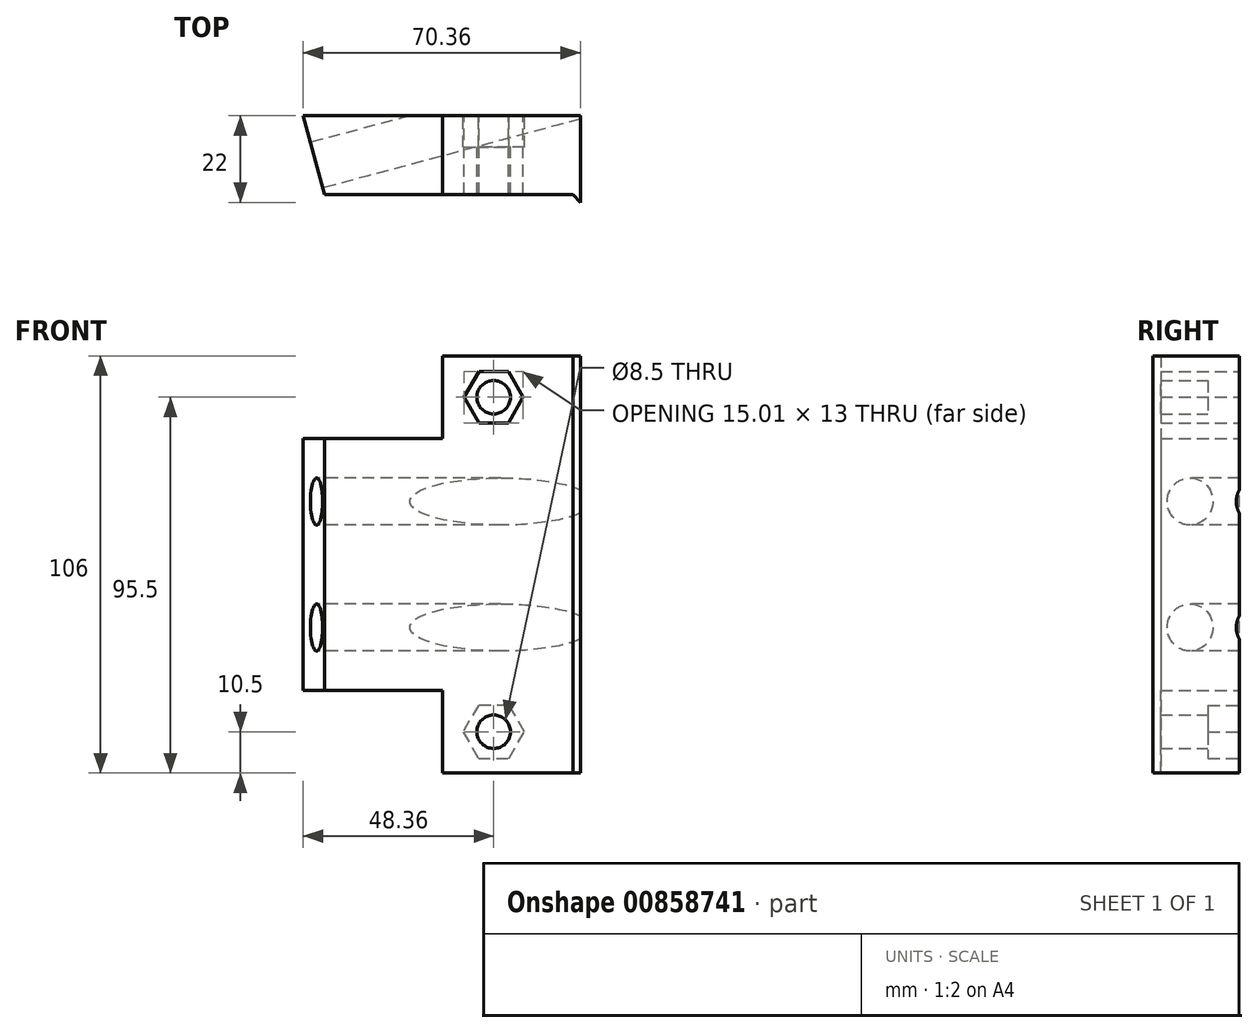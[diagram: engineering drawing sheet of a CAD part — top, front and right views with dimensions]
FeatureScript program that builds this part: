
annotation { "Feature Type Name" : "Feature", "Feature Type Description" : "" }
export const myFeature = defineFeature(function(context is Context, id is Id, definition is map)
    precondition{}
    {
        {
            var Q0;
            Q0=qCreatedBy(makeId("Top.planeOp"),FACE);
            var sketch = newSketch(context, id + "F0", { "sketchPlane" : qUnion([Q0])});
            skLineSegment(sketch, "E0", {"start": v(-1.9, 0) * mm, "end": v(-65, 0) * mm});
            skLineSegment(sketch, "E1", {"start": v(-65, 0) * mm, "end": v(-70.36, 20) * mm});
            skLineSegment(sketch, "E2", {"start": v(-70.36, 20) * mm, "end": v(0, 20) * mm});
            skLineSegment(sketch, "E3", {"start": v(-1.9, 0) * mm, "end": v(0, -2) * mm});
            skLineSegment(sketch, "E4", {"start": v(0, 20) * mm, "end": v(0, -2) * mm});
            skSolve(sketch);
        }
        {
            var Q0;
            Q0=makeQuery(id+"F0.imprint","IMPRINT",FACE,{"disambiguationData":[TD([[makeQuery(id+"F0.imprint","IMPRINT",EDGE,{"derivedFrom":sQuery(id+"F0.wireOp",EDGE,"E0")}),-1.0]])]});
            extrude(context, id + "F1", {"entities" : qUnion([Q0]), "depth" : 64 * mm, "offsetDistance" : 25 * mm});
        }
        {
            var Q0;
            Q0=makeQuery(id+"F1.opExtrude","SWEPT_FACE",FACE,{"disambiguationData":[OSD([sQuery(id+"F0.wireOp",EDGE,"E1")])]});
            var sketch = newSketch(context, id + "F2", { "sketchPlane" : qUnion([Q0])});
            skLineSegment(sketch, "E5", {"start": v(-24.53, 64) * mm, "end": v(-24.53, 0) * mm});
            skLineSegment(sketch, "E6", {"start": v(-24.53, 16) * mm, "end": v(-48.69, 16) * mm});
            skLineSegment(sketch, "E7", {"start": v(-48.69, 16) * mm, "end": v(-48.69, 48) * mm});
            skLineSegment(sketch, "E8", {"start": v(-48.69, 48) * mm, "end": v(-24.53, 48) * mm});
            skSolve(sketch);
        }
        {
            var Q0;
            Q0=sQuery(id+"F2.wireOp",VERTEX,"E8.end");
            var Q1;
            Q1=sQuery(id+"F2.wireOp",VERTEX,"E6.start");
            var Q2;
            Q2=makeQuery(id+"F1.opExtrude","SWEPT_BODY",BODY,{"disambiguationData":[OSD([sQuery(id+"F0.wireOp",EDGE,"E0"),sQuery(id+"F0.wireOp",EDGE,"E1"),sQuery(id+"F0.wireOp",EDGE,"E2"),sQuery(id+"F0.wireOp",EDGE,"E3"),sQuery(id+"F0.wireOp",EDGE,"E4")])]});
            hole(context, id + "F3", {"style" : HoleStyle.SIMPLE, "endStyle" : HoleEndStyle.THROUGH, "holeDiameter" : 12 * mm, "majorDiameter" : 5 * mm, "isTappedThrough" : true, "tappedDepth" : 12 * mm, "tapClearance" : 3, "locations" : qUnion([Q0, Q1]), "scope" : qUnion([Q2])});
        }
        {
            var Q0;
            Q0=makeQuery(id+"F1.opExtrude","CAP_FACE",FACE,{"disambiguationData":[OSD([sQuery(id+"F0.wireOp",EDGE,"E0"),sQuery(id+"F0.wireOp",EDGE,"E1"),sQuery(id+"F0.wireOp",EDGE,"E2"),sQuery(id+"F0.wireOp",EDGE,"E3"),sQuery(id+"F0.wireOp",EDGE,"E4")])],"isStart":true});
            var sketch = newSketch(context, id + "F4", { "sketchPlane" : qUnion([Q0])});
            skLineSegment(sketch, "E9.bottom", {"start": v(0, -20) * mm, "end": v(-35, -20) * mm});
            skLineSegment(sketch, "E9.top", {"start": v(0, 0) * mm, "end": v(-35, 0) * mm});
            skLineSegment(sketch, "E9.left", {"start": v(0, -20) * mm, "end": v(0, 0) * mm});
            skLineSegment(sketch, "E9.right", {"start": v(-35, -20) * mm, "end": v(-35, 0) * mm});
            skSolve(sketch);
        }
        {
            var Q0;
            Q0=makeQuery(id+"F4.imprint","IMPRINT",FACE,{"disambiguationData":[TD([[makeQuery(id+"F4.imprint","IMPRINT",EDGE,{"derivedFrom":sQuery(id+"F4.wireOp",EDGE,"E9.bottom")}),1.0]])]});
            var Q1;
            {var subQ1=makeQuery(id+"F1.opExtrude","CAP_EDGE",EDGE,{"disambiguationData":[OSD([sQuery(id+"F0.wireOp",EDGE,"E3")])],"isStart":true});Q1=makeQuery(id+"F4.imprint","IMPRINT",FACE,{"disambiguationData":[TD([[makeQuery(id+"F4.imprint","IMPRINT",EDGE,{"derivedFrom":subQ1}),-1.0]])]});}
            extrude(context, id + "F5", {"entities" : qUnion([Q0, Q1]), "operationType" : NewBodyOperationType.ADD, "depth" : 21 * mm, "offsetDistance" : 25 * mm});
        }
        {
            var Q0;
            Q0=makeQuery(id+"F5.boolean.opBoolean","MERGE",FACE,{"derivedFrom":[makeQuery(id+"F1.opExtrude","SWEPT_FACE",FACE,{"disambiguationData":[OSD([sQuery(id+"F0.wireOp",EDGE,"E2")])]}),makeQuery(id+"F5.opExtrude","SWEPT_FACE",FACE,{"disambiguationData":[OSD([sQuery(id+"F4.wireOp",EDGE,"E9.bottom")])]})]});
            var sketch = newSketch(context, id + "F6", { "sketchPlane" : qUnion([Q0])});
            skLineSegment(sketch, "E10", {"start": v(35, -10.5) * mm, "end": v(0, -10.5) * mm});
            skLineSegment(sketch, "E11", {"start": v(22, -10.5) * mm, "end": v(22, -21) * mm});
            skCircle(sketch, "E12.cCircle", {"center": v(22, -10.5) * mm, "radius": 6.75 * mm, "construction": true});
            skLineSegment(sketch, "E12.0", {"start": v(25.9, -17.25) * mm, "end": v(18.1, -17.25) * mm});
            skLineSegment(sketch, "E12.1", {"start": v(18.1, -17.25) * mm, "end": v(14.2, -10.5) * mm});
            skLineSegment(sketch, "E12.2", {"start": v(14.2, -10.5) * mm, "end": v(18.1, -3.75) * mm});
            skLineSegment(sketch, "E12.3", {"start": v(18.1, -3.75) * mm, "end": v(25.9, -3.75) * mm});
            skLineSegment(sketch, "E12.4", {"start": v(25.9, -3.75) * mm, "end": v(29.8, -10.5) * mm});
            skLineSegment(sketch, "E12.5", {"start": v(29.8, -10.5) * mm, "end": v(25.9, -17.25) * mm});
            skPoint(sketch, "E12.0.midPoint", {"position": v(22, -17.25) * mm});
            skSolve(sketch);
        }
        {
            var Q0;
            {var subQ3=sQuery(id+"F6.wireOp",EDGE,"E12.5");Q0=makeQuery(id+"F6.imprint","IMPRINT",FACE,{"disambiguationData":[TD([[makeQuery(id+"F6.imprint","IMPRINT",EDGE,{"derivedFrom":subQ3}),-1.0]])]});}
            var Q1;
            {var subQ0=sQuery(id+"F6.wireOp",EDGE,"E12.2");Q1=makeQuery(id+"F6.imprint","IMPRINT",FACE,{"disambiguationData":[TD([[makeQuery(id+"F6.imprint","IMPRINT",EDGE,{"derivedFrom":subQ0}),-1.0]])]});}
            var Q2;
            {var subQ3=sQuery(id+"F6.wireOp",EDGE,"E12.1");Q2=makeQuery(id+"F6.imprint","IMPRINT",FACE,{"disambiguationData":[TD([[makeQuery(id+"F6.imprint","IMPRINT",EDGE,{"derivedFrom":subQ3}),-1.0]])]});}
            extrude(context, id + "F7", {"entities" : qUnion([Q0, Q1, Q2]), "operationType" : NewBodyOperationType.REMOVE, "oppositeDirection" : true, "depth" : 8 * mm, "offsetDistance" : 25 * mm});
        }
        {
            var Q0;
            Q0=makeQuery(id+"F1.opExtrude","CAP_FACE",FACE,{"disambiguationData":[OSD([sQuery(id+"F0.wireOp",EDGE,"E0"),sQuery(id+"F0.wireOp",EDGE,"E1"),sQuery(id+"F0.wireOp",EDGE,"E2"),sQuery(id+"F0.wireOp",EDGE,"E3"),sQuery(id+"F0.wireOp",EDGE,"E4")])],"isStart":false});
            var sketch = newSketch(context, id + "F8", { "sketchPlane" : qUnion([Q0])});
            skLineSegment(sketch, "E13.bottom", {"start": v(0, 20) * mm, "end": v(-35, 20) * mm});
            skLineSegment(sketch, "E13.top", {"start": v(0, 0) * mm, "end": v(-35, 0) * mm});
            skLineSegment(sketch, "E13.left", {"start": v(0, 20) * mm, "end": v(0, 0) * mm});
            skLineSegment(sketch, "E13.right", {"start": v(-35, 20) * mm, "end": v(-35, 0) * mm});
            skSolve(sketch);
        }
        {
            var Q0;
            Q0=makeQuery(id+"F8.imprint","IMPRINT",FACE,{"disambiguationData":[TD([[makeQuery(id+"F8.imprint","IMPRINT",EDGE,{"derivedFrom":sQuery(id+"F8.wireOp",EDGE,"E13.bottom")}),-1.0]])]});
            var Q1;
            {var subQ1=makeQuery(id+"F1.opExtrude","CAP_EDGE",EDGE,{"disambiguationData":[OSD([sQuery(id+"F0.wireOp",EDGE,"E3")])],"isStart":false});Q1=makeQuery(id+"F8.imprint","IMPRINT",FACE,{"disambiguationData":[TD([[makeQuery(id+"F8.imprint","IMPRINT",EDGE,{"derivedFrom":subQ1}),1.0]])]});}
            extrude(context, id + "F9", {"entities" : qUnion([Q0, Q1]), "operationType" : NewBodyOperationType.ADD, "depth" : 21 * mm, "offsetDistance" : 25 * mm});
        }
        {
            var Q0;
            Q0=makeQuery(id+"F9.boolean.opBoolean","MERGE",FACE,{"derivedFrom":[makeQuery(id+"F5.boolean.opBoolean","MERGE",FACE,{"derivedFrom":[makeQuery(id+"F1.opExtrude","SWEPT_FACE",FACE,{"disambiguationData":[OSD([sQuery(id+"F0.wireOp",EDGE,"E2")])]}),makeQuery(id+"F5.opExtrude","SWEPT_FACE",FACE,{"disambiguationData":[OSD([sQuery(id+"F4.wireOp",EDGE,"E9.bottom")])]})]}),makeQuery(id+"F9.opExtrude","SWEPT_FACE",FACE,{"disambiguationData":[OSD([sQuery(id+"F8.wireOp",EDGE,"E13.bottom")])]})]});
            var sketch = newSketch(context, id + "F10", { "sketchPlane" : qUnion([Q0])});
            skLineSegment(sketch, "E14", {"start": v(35, 74.5) * mm, "end": v(0, 74.5) * mm});
            skCircle(sketch, "E15.cCircle", {"center": v(22, 74.5) * mm, "radius": 6.5 * mm, "construction": true});
            skPoint(sketch, "E15.cCircle.centerSnap0", {"position": v(22, -17.25) * mm});
            skLineSegment(sketch, "E15.0", {"start": v(25.75, 68) * mm, "end": v(18.25, 68) * mm});
            skLineSegment(sketch, "E15.1", {"start": v(18.25, 68) * mm, "end": v(14.5, 74.5) * mm});
            skLineSegment(sketch, "E15.2", {"start": v(14.5, 74.5) * mm, "end": v(18.25, 81) * mm});
            skLineSegment(sketch, "E15.3", {"start": v(18.25, 81) * mm, "end": v(25.75, 81) * mm});
            skLineSegment(sketch, "E15.4", {"start": v(25.75, 81) * mm, "end": v(29.5, 74.5) * mm});
            skLineSegment(sketch, "E15.5", {"start": v(29.5, 74.5) * mm, "end": v(25.75, 68) * mm});
            skPoint(sketch, "E15.0.midPoint", {"position": v(22, 68) * mm});
            skSolve(sketch);
        }
        {
            var Q0;
            Q0=makeQuery(id+"F10.imprint","IMPRINT",FACE,{"disambiguationData":[TD([[makeQuery(id+"F10.imprint","IMPRINT",EDGE,{"derivedFrom":sQuery(id+"F10.wireOp",EDGE,"E15.0")}),-1.0]])]});
            var Q1;
            {var subQ0=sQuery(id+"F10.wireOp",EDGE,"E15.2");Q1=makeQuery(id+"F10.imprint","IMPRINT",FACE,{"disambiguationData":[TD([[makeQuery(id+"F10.imprint","IMPRINT",EDGE,{"derivedFrom":subQ0}),-1.0]])]});}
            extrude(context, id + "F11", {"entities" : qUnion([Q0, Q1]), "operationType" : NewBodyOperationType.REMOVE, "oppositeDirection" : true, "depth" : 8 * mm, "offsetDistance" : 25 * mm});
        }
        {
            var Q0;
            Q0=makeQuery(id+"F11.boolean.opBoolean","COPY",FACE,{"derivedFrom":makeQuery(id+"F11.opExtrude","CAP_FACE",FACE,{"disambiguationData":[OSD([sQuery(id+"F10.wireOp",EDGE,"E15.0"),sQuery(id+"F10.wireOp",EDGE,"E15.1"),sQuery(id+"F10.wireOp",EDGE,"E15.2"),sQuery(id+"F10.wireOp",EDGE,"E15.3"),sQuery(id+"F10.wireOp",EDGE,"E15.4"),sQuery(id+"F10.wireOp",EDGE,"E15.5")])],"isStart":false})});
            var sketch = newSketch(context, id + "F12", { "sketchPlane" : qUnion([Q0])});
            skLineSegment(sketch, "E16", {"start": v(25.75, 81) * mm, "end": v(18.25, 68) * mm});
            skCircle(sketch, "E17", {"center": v(22, 74.5) * mm, "radius": 4.25 * mm});
            skSolve(sketch);
        }
        {
            var Q0;
            {var subQ0=sQuery(id+"F12.wireOp",EDGE,"E17");var subQ1=sQuery(id+"F12.wireOp",EDGE,"E16");var subQ2=makeQuery(id+"F12.imprint","INTERSECT",VERTEX,{"disambiguationData":[OD(0.0)],"derivedFrom":[subQ1,subQ0]});Q0=makeQuery(id+"F12.imprint","IMPRINT",FACE,{"disambiguationData":[TD([[makeQuery(id+"F12.imprint","IMPRINT",EDGE,{"disambiguationData":[TD([[subQ2,-1.0]])],"derivedFrom":subQ1}),-1.0]])]});}
            var Q1;
            {var subQ0=sQuery(id+"F12.wireOp",EDGE,"E17");var subQ1=sQuery(id+"F12.wireOp",EDGE,"E16");var subQ2=makeQuery(id+"F12.imprint","INTERSECT",VERTEX,{"disambiguationData":[OD(0.0)],"derivedFrom":[subQ1,subQ0]});Q1=makeQuery(id+"F12.imprint","IMPRINT",FACE,{"disambiguationData":[TD([[makeQuery(id+"F12.imprint","IMPRINT",EDGE,{"disambiguationData":[TD([[subQ2,-1.0]])],"derivedFrom":subQ1}),1.0]])]});}
            extrude(context, id + "F13", {"entities" : qUnion([Q0, Q1]), "operationType" : NewBodyOperationType.REMOVE, "oppositeDirection" : true, "depth" : 25 * mm, "offsetDistance" : 25 * mm});
        }
        {
            var Q0;
            Q0=sQuery(id+"F6.wireOp",VERTEX,"E11.start");
            var Q1;
            Q1=makeQuery(id+"F1.opExtrude","SWEPT_BODY",BODY,{"disambiguationData":[OSD([sQuery(id+"F0.wireOp",EDGE,"E0"),sQuery(id+"F0.wireOp",EDGE,"E1"),sQuery(id+"F0.wireOp",EDGE,"E2"),sQuery(id+"F0.wireOp",EDGE,"E3"),sQuery(id+"F0.wireOp",EDGE,"E4")])]});
            hole(context, id + "F14", {"style" : HoleStyle.SIMPLE, "endStyle" : HoleEndStyle.THROUGH, "holeDiameter" : 8.5 * mm, "majorDiameter" : 5 * mm, "isTappedThrough" : true, "tappedDepth" : 12 * mm, "tapClearance" : 3, "locations" : qUnion([Q0]), "scope" : qUnion([Q1])});
        }
    });
